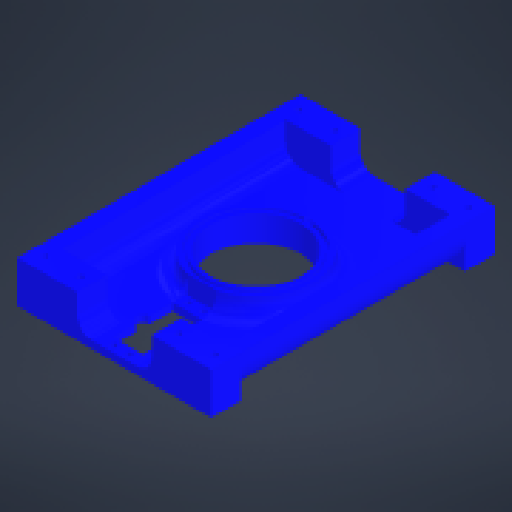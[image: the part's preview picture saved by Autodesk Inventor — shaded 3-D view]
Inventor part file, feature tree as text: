
AUTODESK INVENTOR PART (.ipt)
format: ipt  version: 2024 (Build 280153000, 153)  size: 388,096 bytes
history: native  units: mm
features: other x11, reference x9, extrude x8, sketch x8, projected_geometry x3, mirror x2, imported_body x1
ambient origin geometry x8: Origin, YZ Plane, XZ Plane, XY Plane, X Axis, Y Axis, Z Axis, Center Point
bodies: Body1 (feature_tree)
feature tree (42):
  other  "Твердое тело1"
  extrude  "Выдавливание2"  TaperAngle=0.0deg  [1 undecoded]
  other  "РабПлоскость1"
  other  "РабПлоскость2"
  mirror  "Зеркальное отражение1"
  mirror  "Зеркальное отражение2"
  extrude  "Выдавливание1"  Depth=20.0mm TaperAngle=0.0deg
  extrude  "Выдавливание3"  Depth=2.0mm
  extrude  "Выдавливание4"  Depth=60.5mm
  extrude  "Выдавливание5"  Depth=38.0mm
  extrude  "Выдавливание6"  Depth=2.875mm
  extrude  "Выдавливание7"  Depth=3.0mm TaperAngle=0.0deg
  extrude  "Выдавливание8"  Depth=3.0mm TaperAngle=0.0deg
  sketch  "Эскиз1"
  reference  "Ссылка1"
  reference  "Ссылка2"
  reference  "Ссылка3"
  reference  "Ссылка4"
  reference  "Ссылка5"
  reference  "Ссылка6"
  reference  "Ссылка7"
  reference  "Ссылка8"
  sketch  "Эскиз2"
  sketch  "Эскиз3"
  sketch  "Эскиз4"
  projected_geometry  "Спроецированная петля1"
  sketch  "Эскиз5"
  sketch  "Эскиз6"
  sketch  "Эскиз7"
  projected_geometry  "Спроецированная петля2"
  projected_geometry  "Спроецированная петля3"
  sketch  "Эскиз8"
  reference  "Ссылка9"
  imported_body  "БазТело1"
  parser-record x2  (decoder bookkeeping rows leaked as tree rows — omitted from the tree; the rows remain in map.json)
  other  "main_assembly.iam"
  other  "base_assambly:1"
  other  "side_axis:2"
  other  "side_axis:1"
  other  "manipulator.iam"
  other  "servo_40kg:1"
note: 1 required parameter value undecoded (feature->parameter linkage not recoverable at this tier; creation-order binding heuristic only, values carry confidence <= 0.55)
note: 2 file-system paths scrubbed to <path> (originals preserved in map.json)
